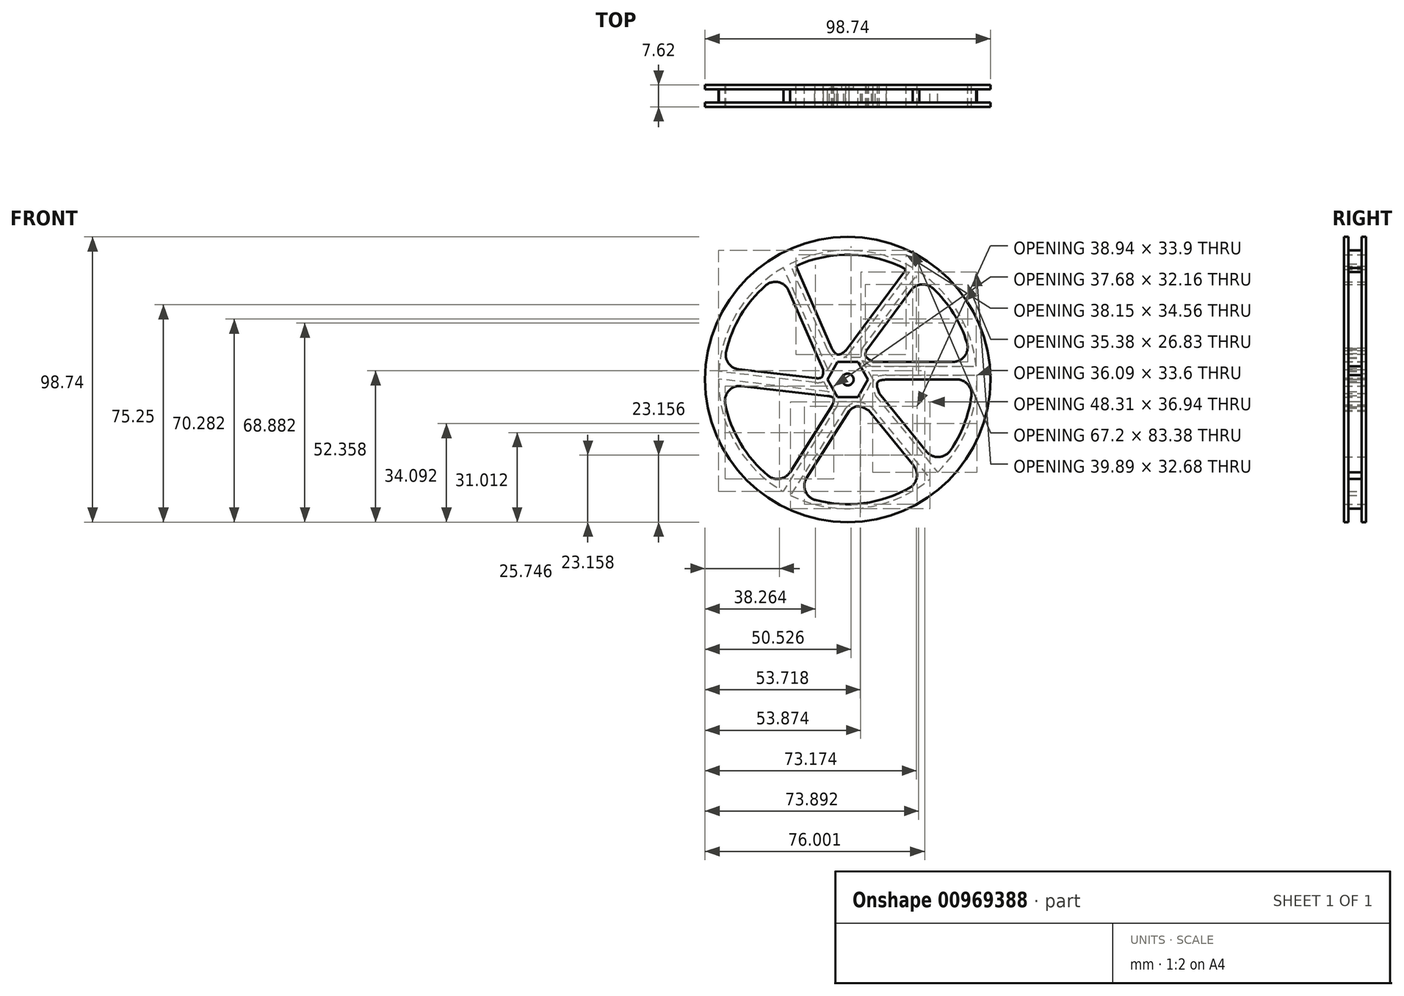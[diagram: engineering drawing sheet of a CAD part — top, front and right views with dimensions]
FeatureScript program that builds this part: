
annotation { "Feature Type Name" : "Feature", "Feature Type Description" : "" }
export const myFeature = defineFeature(function(context is Context, id is Id, definition is map)
    precondition{}
    {
        {
            var Q0;
            Q0=qCreatedBy(makeId("Front.planeOp"),FACE);
            var sketch = newSketch(context, id + "F0", { "sketchPlane" : qUnion([Q0])});
            skCircle(sketch, "E0", {"center": v(0, 0) * mm, "radius": 43.18 * mm});
            skLineSegment(sketch, "E1", {"start": v(-3.52, 6.1) * mm, "end": v(3.52, 6.1) * mm});
            skLineSegment(sketch, "E2", {"start": v(3.52, 6.1) * mm, "end": v(7.04, 0) * mm});
            skLineSegment(sketch, "E3", {"start": v(7.04, 0) * mm, "end": v(3.52, -6.1) * mm});
            skLineSegment(sketch, "E4", {"start": v(3.52, -6.1) * mm, "end": v(-3.52, -6.1) * mm});
            skLineSegment(sketch, "E5", {"start": v(-3.52, -6.1) * mm, "end": v(-7.04, 0) * mm});
            skLineSegment(sketch, "E6", {"start": v(-7.04, 0) * mm, "end": v(-3.52, 6.1) * mm});
            skPoint(sketch, "E7.0.internal.snap0", {"position": v(0, 6.1) * mm});
            skPoint(sketch, "E7.2.internal.snap0", {"position": v(0, 6.1) * mm});
            skCircle(sketch, "E8", {"center": v(0, 0) * mm, "radius": 2.03 * mm});
            skCircle(sketch, "E9", {"center": v(0, 0) * mm, "radius": 49.37 * mm});
            skLineSegment(sketch, "E10", {"start": v(-5.28, -3.05) * mm, "end": v(-43.16, 1.3) * mm});
            skLineSegment(sketch, "E11", {"start": v(0, -6.1) * mm, "end": v(-20.29, -38.12) * mm});
            skLineSegment(sketch, "E12", {"start": v(5.28, -3.05) * mm, "end": v(28.88, -32.1) * mm});
            skLineSegment(sketch, "E13", {"start": v(5.28, 3.05) * mm, "end": v(43.07, 3.05) * mm});
            skLineSegment(sketch, "E14", {"start": v(22.7, 36.73) * mm, "end": v(0.67, 7) * mm});
            skLineSegment(sketch, "E15", {"start": v(-5.73, 4.09) * mm, "end": v(-20.46, 38.03) * mm});
            skLineSegment(sketch, "E16", {"start": v(-5.73, 4.09) * mm, "end": v(-5.28, 3.05) * mm});
            skLineSegment(sketch, "E17", {"start": v(0.67, 7) * mm, "end": v(0, 6.1) * mm});
            skFitSpline(sketch, "E18", {"points": [v(-7.15, -5.68) * mm, v(-4.92, -6.41) * mm, v(-5.22, -8.78) * mm], "startDerivative": vector(5.75, -0.66) * mm, "endDerivative": vector(-1.88, -5.53) * mm});
            skLineSegment(sketch, "E19", {"start": v(-5.22, -8.78) * mm, "end": v(-22.86, -36.63) * mm});
            skLineSegment(sketch, "E20", {"start": v(-7.15, -5.68) * mm, "end": v(-43.15, -1.55) * mm});
            skFitSpline(sketch, "E21", {"points": [v(-11.3, 0.49) * mm, v(-8.97, 0.8) * mm, v(-8.54, 3.45) * mm], "startDerivative": vector(5.78, -0.46) * mm, "endDerivative": vector(-0.19, 6.3) * mm});
            skLineSegment(sketch, "E22", {"start": v(-11.3, 0.49) * mm, "end": v(-42.98, 4.12) * mm});
            skLineSegment(sketch, "E23", {"start": v(-8.54, 3.45) * mm, "end": v(-22.92, 36.6) * mm});
            skFitSpline(sketch, "E24", {"points": [v(-5.62, 10.94) * mm, v(-3.44, 8.6) * mm, v(-0.58, 10.07) * mm], "startDerivative": vector(4.04, -6.6) * mm, "endDerivative": vector(6.06, 4.84) * mm});
            skLineSegment(sketch, "E25", {"start": v(-5.62, 10.94) * mm, "end": v(-17.92, 39.29) * mm});
            skLineSegment(sketch, "E26", {"start": v(-0.58, 10.07) * mm, "end": v(20.23, 38.15) * mm});
            skFitSpline(sketch, "E27", {"points": [v(6.46, 10.07) * mm, v(6.19, 8.17) * mm, v(8.82, 6.1) * mm], "startDerivative": vector(-1.77, -4.57) * mm, "endDerivative": vector(6.13, -3.43) * mm});
            skLineSegment(sketch, "E28", {"start": v(6.46, 10.07) * mm, "end": v(25.06, 35.16) * mm});
            skLineSegment(sketch, "E29", {"start": v(8.82, 6.1) * mm, "end": v(42.75, 6.1) * mm});
            skFitSpline(sketch, "E30", {"points": [v(13.42, 0) * mm, v(10.3, -0.98) * mm, v(10.94, -4.8) * mm], "startDerivative": vector(-8.39, -0.77) * mm, "endDerivative": vector(3.26, -8.71) * mm});
            skLineSegment(sketch, "E31", {"start": v(13.42, 0) * mm, "end": v(43.18, 0) * mm});
            skLineSegment(sketch, "E32", {"start": v(10.94, -4.8) * mm, "end": v(31.25, -29.8) * mm});
            skFitSpline(sketch, "E33", {"points": [v(0.47, -10.91) * mm, v(3.17, -9.28) * mm, v(7.23, -10.67) * mm], "startDerivative": vector(5.47, 4.95) * mm, "endDerivative": vector(8, -4.23) * mm});
            skLineSegment(sketch, "E34", {"start": v(7.23, -10.67) * mm, "end": v(26.35, -34.2) * mm});
            skLineSegment(sketch, "E35", {"start": v(0.47, -10.91) * mm, "end": v(-17.6, -39.43) * mm});
            skSolve(sketch);
        }
        {
            var Q0;
            Q0=makeQuery(id+"F0.imprint","IMPRINT",FACE,{"disambiguationData":[TD([[makeQuery(id+"F0.imprint","IMPRINT",EDGE,{"derivedFrom":sQuery(id+"F0.wireOp",EDGE,"E9")}),1.0]])]});
            var Q1;
            {var subQ2=sQuery(id+"F0.wireOp",EDGE,"E14");Q1=makeQuery(id+"F0.imprint","IMPRINT",FACE,{"disambiguationData":[TD([[makeQuery(id+"F0.imprint","IMPRINT",EDGE,{"derivedFrom":subQ2}),-1.0]])]});}
            var Q2;
            {var subQ4=sQuery(id+"F0.wireOp",EDGE,"E10");Q2=makeQuery(id+"F0.imprint","IMPRINT",FACE,{"disambiguationData":[TD([[makeQuery(id+"F0.imprint","IMPRINT",EDGE,{"derivedFrom":subQ4}),-1.0]])]});}
            var Q3;
            {var subQ3=sQuery(id+"F0.wireOp",EDGE,"E13");Q3=makeQuery(id+"F0.imprint","IMPRINT",FACE,{"disambiguationData":[TD([[makeQuery(id+"F0.imprint","IMPRINT",EDGE,{"derivedFrom":subQ3}),1.0]])]});}
            var Q4;
            {var subQ3=sQuery(id+"F0.wireOp",EDGE,"E12");Q4=makeQuery(id+"F0.imprint","IMPRINT",FACE,{"disambiguationData":[TD([[makeQuery(id+"F0.imprint","IMPRINT",EDGE,{"derivedFrom":subQ3}),1.0]])]});}
            var Q5;
            {var subQ3=sQuery(id+"F0.wireOp",EDGE,"E11");Q5=makeQuery(id+"F0.imprint","IMPRINT",FACE,{"disambiguationData":[TD([[makeQuery(id+"F0.imprint","IMPRINT",EDGE,{"derivedFrom":subQ3}),1.0]])]});}
            var Q6;
            {var subQ3=sQuery(id+"F0.wireOp",EDGE,"E10");Q6=makeQuery(id+"F0.imprint","IMPRINT",FACE,{"disambiguationData":[TD([[makeQuery(id+"F0.imprint","IMPRINT",EDGE,{"derivedFrom":subQ3}),1.0]])]});}
            extrude(context, id + "F1", {"entities" : qUnion([Q0, Q1, Q2, Q3, Q4, Q5, Q6]), "depth" : 7.62 * mm, "offsetDistance" : 25.4 * mm});
        }
        {
            var Q0;
            Q0=makeQuery(id+"F0.imprint","IMPRINT",FACE,{"disambiguationData":[TD([[makeQuery(id+"F0.imprint","IMPRINT",EDGE,{"derivedFrom":sQuery(id+"F0.wireOp",EDGE,"E8")}),-1.0]])]});
            extrude(context, id + "F2", {"entities" : qUnion([Q0]), "operationType" : NewBodyOperationType.ADD, "depth" : 1.27 * mm, "offsetDistance" : 25.4 * mm});
        }
        {
            var Q0;
            Q0=makeQuery(id+"F1.opExtrude","SWEPT_FACE",FACE,{"disambiguationData":[OSD([sQuery(id+"F0.wireOp",EDGE,"E9")])]});
            shell(context, id + "F3", {"entities" : qUnion([Q0]), "thickness" : 1.52 * mm});
        }
        {
            var Q0;
            Q0=makeQuery(id+"F1.opExtrude","SWEPT_EDGE",EDGE,{"disambiguationData":[OSD([sQuery(id+"F0.wireOp",EDGE,"E0"),sQuery(id+"F0.wireOp",EDGE,"E31")])]});
            var Q1;
            Q1=makeQuery(id+"F1.opExtrude","SWEPT_EDGE",EDGE,{"disambiguationData":[OSD([sQuery(id+"F0.wireOp",EDGE,"E0"),sQuery(id+"F0.wireOp",EDGE,"E29")])]});
            var Q2;
            Q2=makeQuery(id+"F1.opExtrude","SWEPT_EDGE",EDGE,{"disambiguationData":[OSD([sQuery(id+"F0.wireOp",EDGE,"E0"),sQuery(id+"F0.wireOp",EDGE,"E28")])]});
            var Q3;
            Q3=makeQuery(id+"F1.opExtrude","SWEPT_EDGE",EDGE,{"disambiguationData":[OSD([sQuery(id+"F0.wireOp",EDGE,"E0"),sQuery(id+"F0.wireOp",EDGE,"E32")])]});
            var Q4;
            Q4=makeQuery(id+"F1.opExtrude","SWEPT_EDGE",EDGE,{"disambiguationData":[OSD([sQuery(id+"F0.wireOp",EDGE,"E0"),sQuery(id+"F0.wireOp",EDGE,"E34")])]});
            var Q5;
            Q5=makeQuery(id+"F1.opExtrude","SWEPT_EDGE",EDGE,{"disambiguationData":[OSD([sQuery(id+"F0.wireOp",EDGE,"E0"),sQuery(id+"F0.wireOp",EDGE,"E35")])]});
            var Q6;
            Q6=makeQuery(id+"F1.opExtrude","SWEPT_EDGE",EDGE,{"disambiguationData":[OSD([sQuery(id+"F0.wireOp",EDGE,"E0"),sQuery(id+"F0.wireOp",EDGE,"E19")])]});
            var Q7;
            Q7=makeQuery(id+"F1.opExtrude","SWEPT_EDGE",EDGE,{"disambiguationData":[OSD([sQuery(id+"F0.wireOp",EDGE,"E0"),sQuery(id+"F0.wireOp",EDGE,"E20")])]});
            var Q8;
            Q8=makeQuery(id+"F1.opExtrude","SWEPT_EDGE",EDGE,{"disambiguationData":[OSD([sQuery(id+"F0.wireOp",EDGE,"E0"),sQuery(id+"F0.wireOp",EDGE,"E22")])]});
            var Q9;
            Q9=makeQuery(id+"F1.opExtrude","SWEPT_EDGE",EDGE,{"disambiguationData":[OSD([sQuery(id+"F0.wireOp",EDGE,"E0"),sQuery(id+"F0.wireOp",EDGE,"E23")])]});
            fillet(context, id + "F4", {"entities" : qUnion([Q0, Q1, Q2, Q3, Q4, Q5, Q6, Q7, Q8, Q9]), "radius" : 5.08 * mm, "tangentPropagation" : true, "allowEdgeOverflow" : false});
        }
    });
